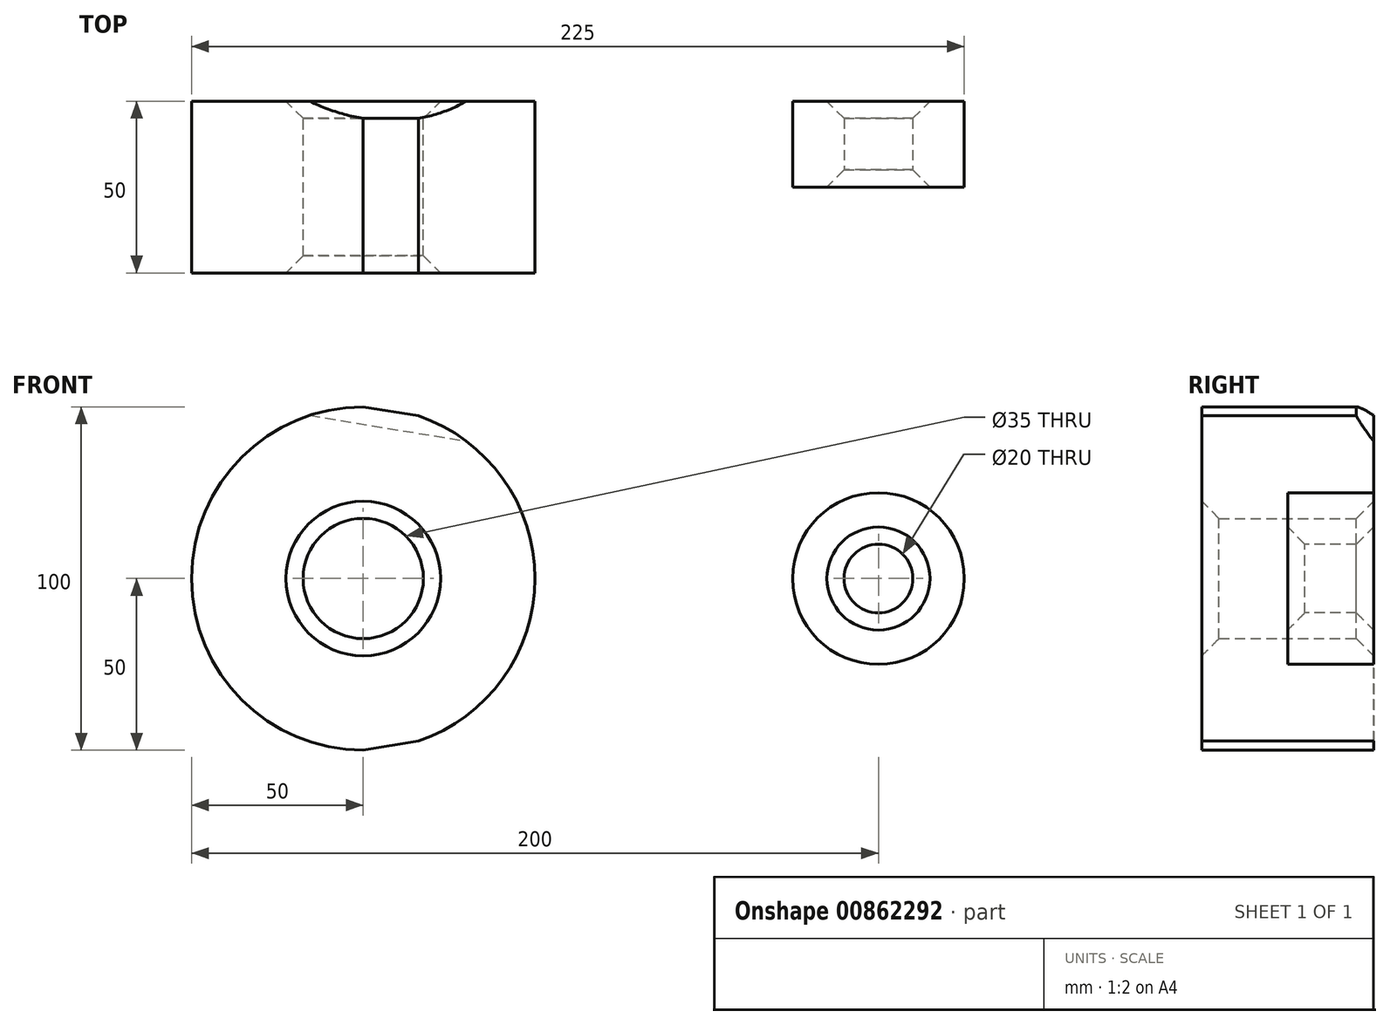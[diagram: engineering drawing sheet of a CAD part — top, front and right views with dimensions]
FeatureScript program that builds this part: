
annotation { "Feature Type Name" : "Feature", "Feature Type Description" : "" }
export const myFeature = defineFeature(function(context is Context, id is Id, definition is map)
    precondition{}
    {
        {
            var Q0;
            Q0=qCreatedBy(makeId("Front.planeOp"),FACE);
            var sketch = newSketch(context, id + "F0", { "sketchPlane" : qUnion([Q0])});
            skCircle(sketch, "E0", {"center": v(0, 0) * mm, "radius": 50 * mm});
            skCircle(sketch, "E1", {"center": v(150, 0) * mm, "radius": 25 * mm});
            skLineSegment(sketch, "E2", {"start": v(0, 50) * mm, "end": v(154.06, 24.67) * mm});
            skLineSegment(sketch, "E3", {"start": v(0, -50) * mm, "end": v(154.06, -24.67) * mm});
            skCircle(sketch, "E4", {"center": v(0, 0) * mm, "radius": 17.5 * mm});
            skCircle(sketch, "E5", {"center": v(150, 0) * mm, "radius": 10 * mm});
            skSolve(sketch);
        }
        {
            var Q0;
            {var subQ0=sQuery(id+"F0.wireOp",EDGE,"E2");var subQ1=sQuery(id+"F0.wireOp",EDGE,"E0");var subQ2=makeQuery(id+"F0.imprint","INTERSECT",VERTEX,{"disambiguationData":[OD(1.0)],"derivedFrom":[subQ1,subQ0]});Q0=makeQuery(id+"F0.imprint","IMPRINT",FACE,{"disambiguationData":[TD([[makeQuery(id+"F0.imprint","IMPRINT",EDGE,{"disambiguationData":[TD([[subQ2,1.0]])],"derivedFrom":subQ1}),-1.0]])]});}
            var Q1;
            Q1=makeQuery(id+"F0.imprint","IMPRINT",FACE,{"disambiguationData":[TD([[makeQuery(id+"F0.imprint","IMPRINT",EDGE,{"derivedFrom":sQuery(id+"F0.wireOp",EDGE,"E5")}),-1.0]])]});
            extrude(context, id + "F1", {"entities" : qUnion([Q0, Q1]), "oppositeDirection" : true, "depth" : 25 * mm, "offsetDistance" : 25 * mm});
        }
        {
            var Q0;
            Q0=makeQuery(id+"F0.imprint","IMPRINT",FACE,{"disambiguationData":[TD([[makeQuery(id+"F0.imprint","IMPRINT",EDGE,{"derivedFrom":sQuery(id+"F0.wireOp",EDGE,"E4")}),-1.0]])]});
            extrude(context, id + "F2", {"entities" : qUnion([Q0]), "operationType" : NewBodyOperationType.ADD, "endBound" : BoundingType.SYMMETRIC, "depth" : 50 * mm, "offsetDistance" : 25 * mm});
        }
        {
            var Q0;
            Q0=makeQuery(id+"F2.opExtrude","CAP_EDGE",EDGE,{"disambiguationData":[OSD([sQuery(id+"F0.wireOp",EDGE,"E4")])],"isStart":false});
            var Q1;
            Q1=makeQuery(id+"F1.opExtrude","CAP_EDGE",EDGE,{"disambiguationData":[OSD([sQuery(id+"F0.wireOp",EDGE,"E5")])],"isStart":false});
            var Q2;
            Q2=makeQuery(id+"F1.opExtrude","CAP_EDGE",EDGE,{"disambiguationData":[OSD([sQuery(id+"F0.wireOp",EDGE,"E5")])],"isStart":true});
            var Q3;
            Q3=makeQuery(id+"F2.opExtrude","CAP_EDGE",EDGE,{"disambiguationData":[OSD([sQuery(id+"F0.wireOp",EDGE,"E4")])],"isStart":true});
            var Q4;
            {var subQ0=sQuery(id+"F0.wireOp",EDGE,"E0");Q4=makeQuery(id+"F2.opExtrude","CAP_EDGE",EDGE,{"disambiguationData":[OSD([subQ0]),TDD([makeQuery(id+"F0.imprint","IMPRINT",EDGE,{"disambiguationData":[TD([[makeQuery(id+"F0.imprint","INTERSECT",VERTEX,{"disambiguationData":[OD(0.0)],"derivedFrom":[subQ0,sQuery(id+"F0.wireOp",EDGE,"E2")]}),-1.0]])],"derivedFrom":subQ0})])],"isStart":false});}
            var Q5;
            {var subQ0=sQuery(id+"F0.wireOp",EDGE,"E0");Q5=makeQuery(id+"F2.opExtrude","CAP_EDGE",EDGE,{"disambiguationData":[OSD([subQ0]),TDD([makeQuery(id+"F0.imprint","IMPRINT",EDGE,{"disambiguationData":[TD([[makeQuery(id+"F0.imprint","INTERSECT",VERTEX,{"disambiguationData":[OD(0.0)],"derivedFrom":[subQ0,sQuery(id+"F0.wireOp",EDGE,"E2")]}),-1.0]])],"derivedFrom":subQ0})])],"isStart":true});}
            var Q6;
            {var subQ0=sQuery(id+"F0.wireOp",EDGE,"E2");Q6=makeQuery(id+"F2.boolean.opBoolean","MERGE",EDGE,{"derivedFrom":[makeQuery(id+"F1.opExtrude","CAP_EDGE",EDGE,{"disambiguationData":[OSD([subQ0])],"isStart":false}),makeQuery(id+"F2.opExtrude","CAP_EDGE",EDGE,{"disambiguationData":[OSD([subQ0])],"isStart":true})]});}
            chamfer(context, id + "F3", {"entities" : qUnion([Q0, Q1, Q2, Q3, Q4, Q5, Q6]), "width" : 5 * mm, "tangentPropagation" : true});
        }
    });
